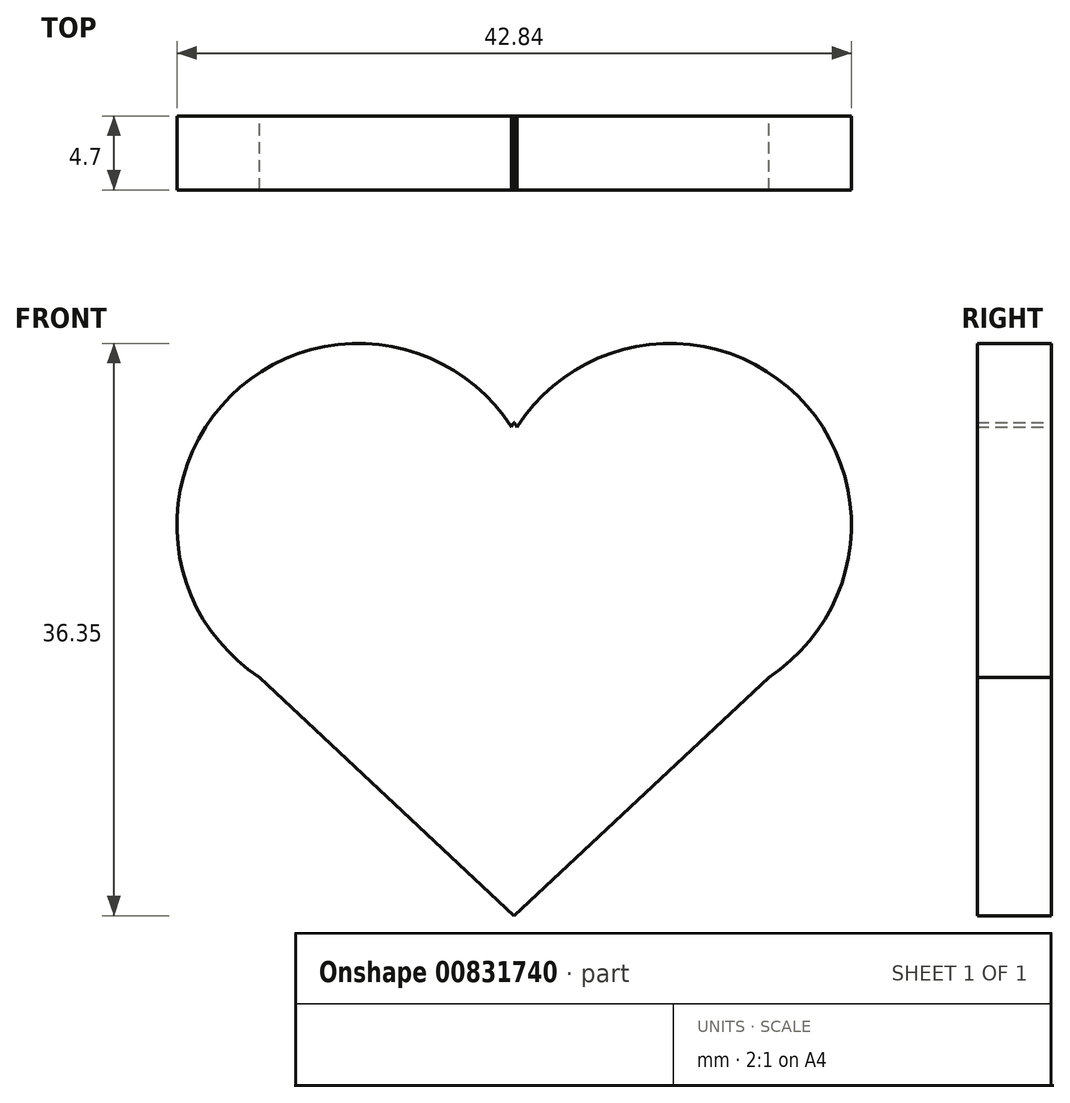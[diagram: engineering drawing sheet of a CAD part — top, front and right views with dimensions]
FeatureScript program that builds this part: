
annotation { "Feature Type Name" : "Feature", "Feature Type Description" : "" }
export const myFeature = defineFeature(function(context is Context, id is Id, definition is map)
    precondition{}
    {
        {
            var Q0;
            Q0=qCreatedBy(makeId("Front.planeOp"),FACE);
            var sketch = newSketch(context, id + "F0", { "sketchPlane" : qUnion([Q0])});
            skArc(sketch, "E0", {"start": v(-0.05, 11.37) * mm, "mid": v(-17.93, 13.61) * mm, "end": v(-16.18, -4.32) * mm});
            skArc(sketch, "E1.1.0", {"start": v(16.24, -3.82) * mm, "mid": v(17.66, 14.15) * mm, "end": v(-0.18, 11.57) * mm});
            skPoint(sketch, "E1.center", {"position": v(-9.89, -14.57) * mm});
            skFitSpline(sketch, "E2", {"points": [v(-16.18, -4.32) * mm, v(0, -19.47) * mm], "startDerivative": vector(16.18, -15.15) * mm, "endDerivative": vector(16.18, -15.15) * mm});
            skFitSpline(sketch, "E3", {"points": [v(16.24, -4.07) * mm, v(0, -19.47) * mm], "startDerivative": vector(-16.21, -15.44) * mm, "endDerivative": vector(-16.21, -15.44) * mm});
            skArc(sketch, "E4.MirrorCS", {"start": v(-16.24, -3.82) * mm, "mid": v(-17.66, 14.15) * mm, "end": v(0.18, 11.57) * mm});
            skFitSpline(sketch, "E5.MirrorCS", {"points": [v(16.18, -4.32) * mm, v(0, -19.47) * mm], "startDerivative": vector(-16.18, -15.15) * mm, "endDerivative": vector(-16.18, -15.15) * mm});
            skArc(sketch, "E6.MirrorCS", {"start": v(0.05, 11.37) * mm, "mid": v(17.93, 13.61) * mm, "end": v(16.18, -4.32) * mm});
            skSolve(sketch);
        }
        {
            var Q0;
            {var subQ5=sQuery(id+"F0.wireOp",EDGE,"E2");Q0=makeQuery(id+"F0.imprint","IMPRINT",FACE,{"disambiguationData":[TD([[makeQuery(id+"F0.imprint","IMPRINT",EDGE,{"derivedFrom":subQ5}),1.0]])]});}
            extrude(context, id + "F1", {"entities" : qUnion([Q0]), "depth" : 4.7 * mm, "offsetDistance" : 25 * mm});
        }
    });
